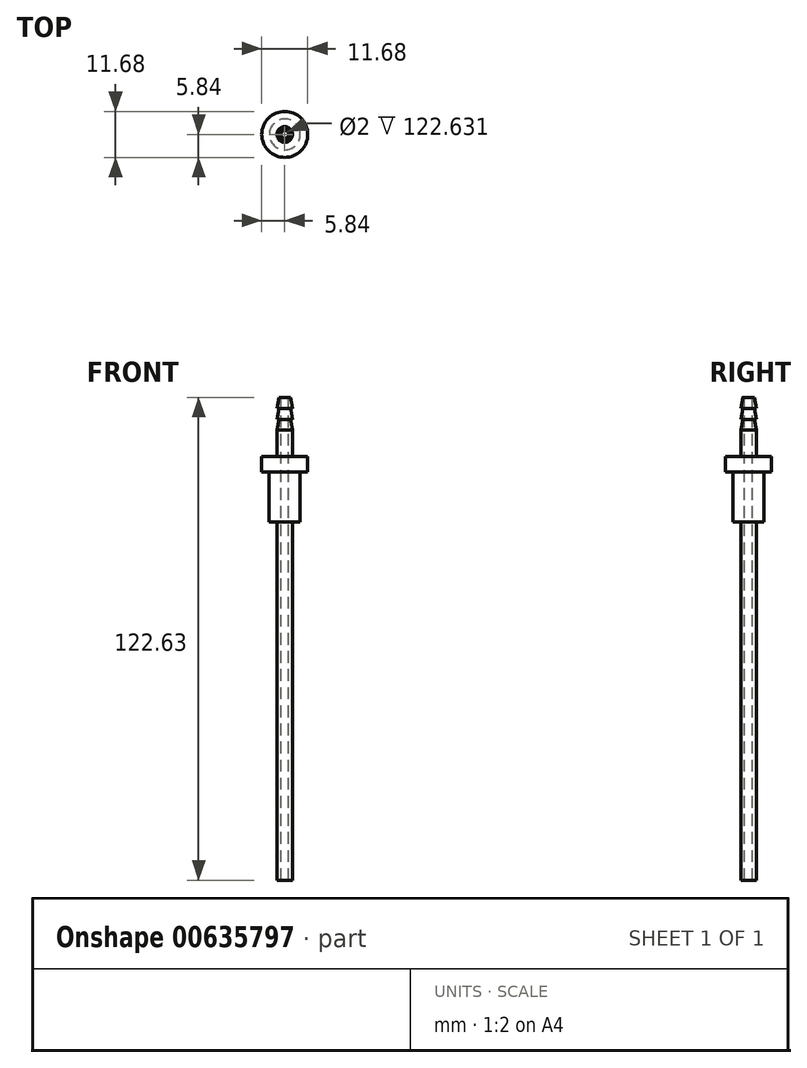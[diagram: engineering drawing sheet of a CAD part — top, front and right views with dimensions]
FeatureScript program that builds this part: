
annotation { "Feature Type Name" : "Feature", "Feature Type Description" : "" }
export const myFeature = defineFeature(function(context is Context, id is Id, definition is map)
    precondition{}
    {
        {
            var Q0;
            Q0=qCreatedBy(makeId("Front.planeOp"),FACE);
            var sketch = newSketch(context, id + "F0", { "sketchPlane" : qUnion([Q0])});
            skLineSegment(sketch, "E0", {"start": v(0, 54.88) * mm, "end": v(0, -67.75) * mm});
            skLineSegment(sketch, "E1", {"start": v(0, -67.75) * mm, "end": v(1.98, -67.75) * mm});
            skLineSegment(sketch, "E2", {"start": v(1.98, -67.75) * mm, "end": v(1.98, 23.24) * mm});
            skLineSegment(sketch, "E3", {"start": v(1.98, 23.24) * mm, "end": v(3.94, 23.24) * mm});
            skLineSegment(sketch, "E4", {"start": v(3.94, 23.24) * mm, "end": v(3.94, 35.94) * mm});
            skLineSegment(sketch, "E5", {"start": v(3.94, 35.94) * mm, "end": v(5.84, 35.94) * mm});
            skLineSegment(sketch, "E6", {"start": v(5.84, 35.94) * mm, "end": v(5.84, 39.9) * mm});
            skLineSegment(sketch, "E7", {"start": v(5.84, 39.9) * mm, "end": v(1.98, 39.9) * mm});
            skLineSegment(sketch, "E8", {"start": v(0, 54.88) * mm, "end": v(1.5, 54.88) * mm});
            skLineSegment(sketch, "E9", {"start": v(1.5, 54.88) * mm, "end": v(1.98, 52.12) * mm});
            skLineSegment(sketch, "E10", {"start": v(1.98, 52.12) * mm, "end": v(1.5, 52.12) * mm});
            skLineSegment(sketch, "E11", {"start": v(1.5, 52.12) * mm, "end": v(1.98, 49.35) * mm});
            skLineSegment(sketch, "E12", {"start": v(1.98, 49.35) * mm, "end": v(1.5, 49.35) * mm});
            skLineSegment(sketch, "E13", {"start": v(1.5, 49.35) * mm, "end": v(1.98, 46.58) * mm});
            skLineSegment(sketch, "E14", {"start": v(1.98, 46.58) * mm, "end": v(1.98, 39.9) * mm});
            skSolve(sketch);
        }
        {
            var Q0;
            Q0 = qSketchRegion(id + "F0", true);
            var Q1;
            Q1=sQuery(id+"F0.wireOp",EDGE,"E0");
            revolve(context, id + "F1", {"entities" : qUnion([Q0]), "axis" : qUnion([Q1]), "revolveType" : RevolveType.FULL});
        }
        {
            var Q0;
            Q0=makeQuery(id+"F1.opRevolve","SWEPT_FACE",FACE,{"disambiguationData":[OSD([sQuery(id+"F0.wireOp",EDGE,"E8")])]});
            var sketch = newSketch(context, id + "F2", { "sketchPlane" : qUnion([Q0])});
            skCircle(sketch, "E15", {"center": v(0, 0) * mm, "radius": 1 * mm});
            skSolve(sketch);
        }
        {
            var Q0;
            Q0 = qSketchRegion(id + "F2", true);
            extrude(context, id + "F3", {"entities" : qUnion([Q0]), "operationType" : NewBodyOperationType.REMOVE, "endBound" : BoundingType.THROUGH_ALL, "oppositeDirection" : true, "depth" : 25 * mm, "offsetDistance" : 25 * mm});
        }
    });
